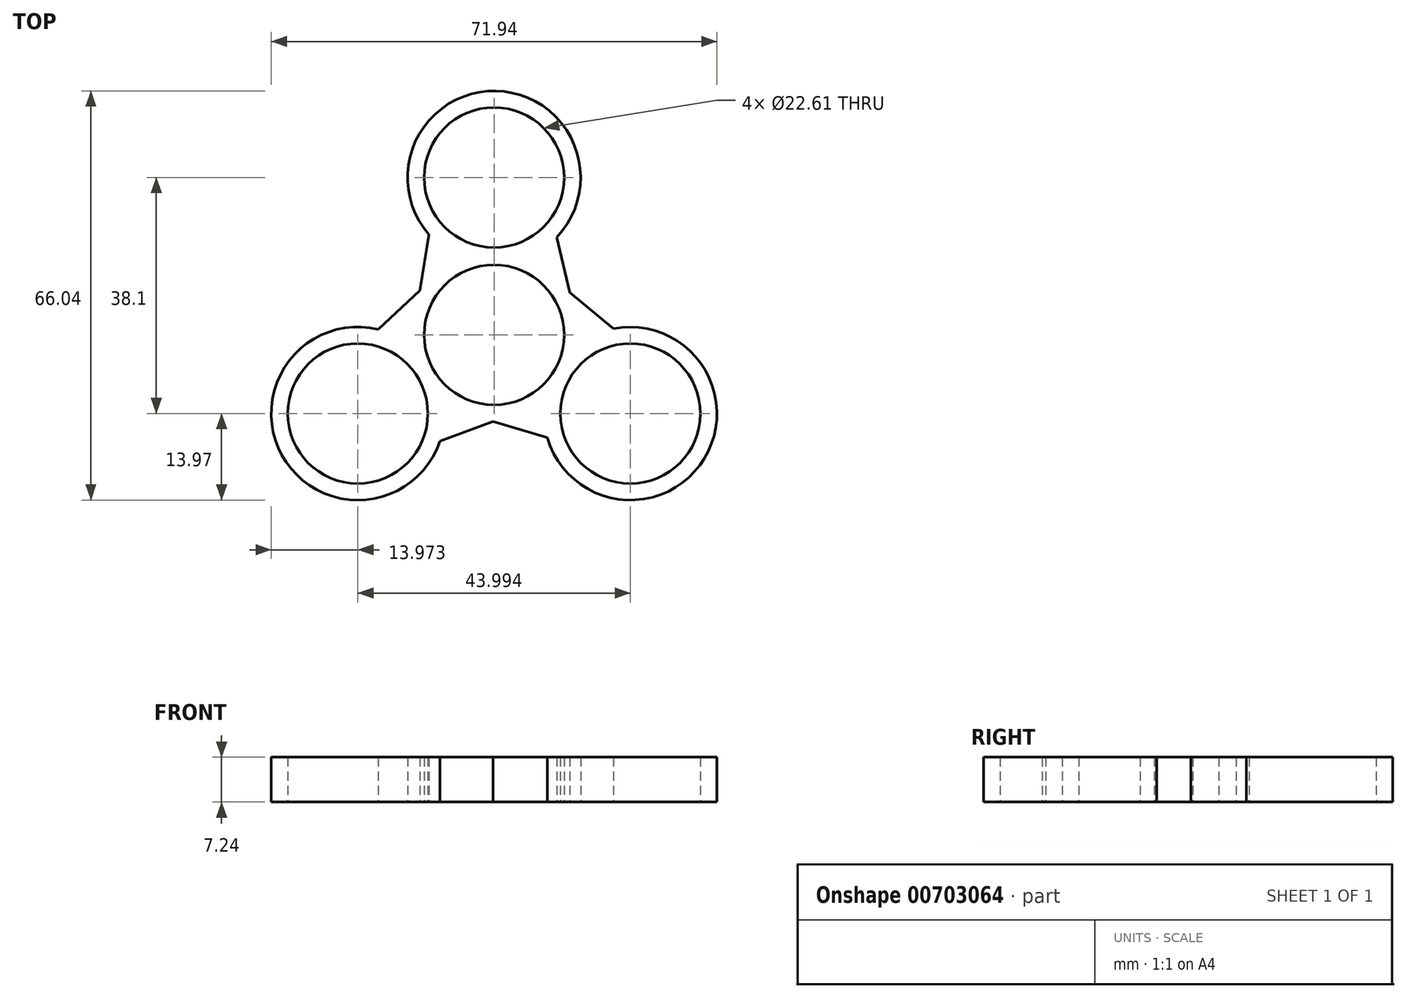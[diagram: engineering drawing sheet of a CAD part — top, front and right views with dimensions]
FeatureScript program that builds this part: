
annotation { "Feature Type Name" : "Feature", "Feature Type Description" : "" }
export const myFeature = defineFeature(function(context is Context, id is Id, definition is map)
    precondition{}
    {
        {
            var Q0;
            Q0=qCreatedBy(makeId("Top.planeOp"),FACE);
            var sketch = newSketch(context, id + "F0", { "sketchPlane" : qUnion([Q0])});
            skCircle(sketch, "E0", {"center": v(0, 25.4) * mm, "radius": 11.3 * mm});
            skCircle(sketch, "E1.1.0", {"center": v(-22, -12.7) * mm, "radius": 11.3 * mm});
            skCircle(sketch, "E1.2.0", {"center": v(22, -12.7) * mm, "radius": 11.3 * mm});
            skPoint(sketch, "E1.center", {"position": v(0, 0) * mm});
            skCircle(sketch, "E2", {"center": v(0, 0) * mm, "radius": 13.97 * mm});
            skPoint(sketch, "E3", {"position": v(-12, 7.14) * mm});
            skPoint(sketch, "E4", {"position": v(-10.18, 18.03) * mm});
            skPoint(sketch, "E5", {"position": v(-19.93, -0.3) * mm});
            skPoint(sketch, "E6.1.0", {"position": v(-10.53, -17.83) * mm});
            skPoint(sketch, "E6.1.1", {"position": v(-0.18, -13.97) * mm});
            skPoint(sketch, "E6.1.2", {"position": v(10.23, -17.1) * mm});
            skPoint(sketch, "E6.2.0", {"position": v(20.7, -0.2) * mm});
            skPoint(sketch, "E6.2.1", {"position": v(12.19, 6.83) * mm});
            skPoint(sketch, "E6.2.2", {"position": v(9.7, 17.42) * mm});
            skLineSegment(sketch, "E7", {"start": v(-12, 7.14) * mm, "end": v(-10.18, 18.03) * mm});
            skLineSegment(sketch, "E8", {"start": v(-12, 7.14) * mm, "end": v(-19.93, -0.3) * mm});
            skLineSegment(sketch, "E9", {"start": v(-10.53, -17.83) * mm, "end": v(-0.18, -13.97) * mm});
            skLineSegment(sketch, "E10", {"start": v(-0.18, -13.97) * mm, "end": v(10.23, -17.1) * mm});
            skLineSegment(sketch, "E11", {"start": v(20.7, -0.2) * mm, "end": v(12.19, 6.83) * mm});
            skLineSegment(sketch, "E12", {"start": v(9.7, 17.42) * mm, "end": v(12.19, 6.83) * mm});
            skCircle(sketch, "E13", {"center": v(0, 0) * mm, "radius": 11.3 * mm});
            skCircle(sketch, "E14", {"center": v(0, 25.4) * mm, "radius": 13.97 * mm});
            skCircle(sketch, "E15.1.0", {"center": v(-22, -12.7) * mm, "radius": 13.97 * mm});
            skCircle(sketch, "E15.2.0", {"center": v(22, -12.7) * mm, "radius": 13.97 * mm});
            skSolve(sketch);
        }
        {
            var Q0;
            Q0=makeQuery(id+"F0.imprint","IMPRINT",FACE,{"disambiguationData":[TD([[makeQuery(id+"F0.imprint","IMPRINT",EDGE,{"derivedFrom":sQuery(id+"F0.wireOp",EDGE,"E0")}),-1.0]])]});
            var Q1;
            {var subQ0=sQuery(id+"F0.wireOp",EDGE,"gAJnjUwW-bYsI-lxhw-ExFC-0EqGxPt0lFPb");Q1=makeQuery(id+"F0.imprint","IMPRINT",FACE,{"disambiguationData":[TD([[makeQuery(id+"F0.imprint","IMPRINT",EDGE,{"derivedFrom":subQ0}),1.0]])]});}
            var Q2;
            {var subQ0=sQuery(id+"F0.wireOp",EDGE,"cbf1ee79-b63b-43e7-bdae-fea5953c93ed.1.1");Q2=makeQuery(id+"F0.imprint","IMPRINT",FACE,{"disambiguationData":[TD([[makeQuery(id+"F0.imprint","IMPRINT",EDGE,{"derivedFrom":subQ0}),1.0]])]});}
            var Q3;
            Q3=makeQuery(id+"F0.imprint","IMPRINT",FACE,{"disambiguationData":[TD([[makeQuery(id+"F0.imprint","IMPRINT",EDGE,{"derivedFrom":sQuery(id+"F0.wireOp",EDGE,"LQtzWtV1-cpov-eoDI-daBr-TH9JdLP4XcMI")}),-1.0]])]});
            var Q4;
            Q4=makeQuery(id+"F0.imprint","IMPRINT",FACE,{"disambiguationData":[TD([[makeQuery(id+"F0.imprint","IMPRINT",EDGE,{"derivedFrom":sQuery(id+"F0.wireOp",EDGE,"LQtzWtV1-cpov-eoDI-daBr-TH9JdLP4XcMI")}),1.0]])]});
            var Q5;
            Q5=makeQuery(id+"F0.imprint","IMPRINT",FACE,{"disambiguationData":[TD([[makeQuery(id+"F0.imprint","IMPRINT",EDGE,{"derivedFrom":sQuery(id+"F0.wireOp",EDGE,"E1.2.0")}),-1.0]])]});
            var Q6;
            Q6=makeQuery(id+"F0.imprint","IMPRINT",FACE,{"disambiguationData":[TD([[makeQuery(id+"F0.imprint","IMPRINT",EDGE,{"derivedFrom":sQuery(id+"F0.wireOp",EDGE,"E1.1.0")}),-1.0]])]});
            var Q7;
            {var subQ0=sQuery(id+"F0.wireOp",EDGE,"XxgCCsIO-ZqaA-fPwp-7T2X-JmL23n1TTZja");Q7=makeQuery(id+"F0.imprint","IMPRINT",FACE,{"disambiguationData":[TD([[makeQuery(id+"F0.imprint","IMPRINT",EDGE,{"derivedFrom":subQ0}),1.0]])]});}
            var Q8;
            Q8=makeQuery(id+"F0.imprint","IMPRINT",FACE,{"disambiguationData":[TD([[makeQuery(id+"F0.imprint","IMPRINT",EDGE,{"derivedFrom":sQuery(id+"F0.wireOp",EDGE,"E13")}),-1.0]])]});
            var Q9;
            {var subQ0=sQuery(id+"F0.wireOp",EDGE,"E8");Q9=makeQuery(id+"F0.imprint","IMPRINT",FACE,{"disambiguationData":[TD([[makeQuery(id+"F0.imprint","IMPRINT",EDGE,{"derivedFrom":subQ0}),1.0]])]});}
            var Q10;
            {var subQ0=sQuery(id+"F0.wireOp",EDGE,"E7");Q10=makeQuery(id+"F0.imprint","IMPRINT",FACE,{"disambiguationData":[TD([[makeQuery(id+"F0.imprint","IMPRINT",EDGE,{"derivedFrom":subQ0}),-1.0]])]});}
            var Q11;
            {var subQ0=sQuery(id+"F0.wireOp",EDGE,"E12");Q11=makeQuery(id+"F0.imprint","IMPRINT",FACE,{"disambiguationData":[TD([[makeQuery(id+"F0.imprint","IMPRINT",EDGE,{"derivedFrom":subQ0}),-1.0]])]});}
            var Q12;
            {var subQ0=sQuery(id+"F0.wireOp",EDGE,"E11");Q12=makeQuery(id+"F0.imprint","IMPRINT",FACE,{"disambiguationData":[TD([[makeQuery(id+"F0.imprint","IMPRINT",EDGE,{"derivedFrom":subQ0}),1.0]])]});}
            var Q13;
            {var subQ0=sQuery(id+"F0.wireOp",EDGE,"E10");Q13=makeQuery(id+"F0.imprint","IMPRINT",FACE,{"disambiguationData":[TD([[makeQuery(id+"F0.imprint","IMPRINT",EDGE,{"derivedFrom":subQ0}),1.0]])]});}
            var Q14;
            {var subQ0=sQuery(id+"F0.wireOp",EDGE,"E9");Q14=makeQuery(id+"F0.imprint","IMPRINT",FACE,{"disambiguationData":[TD([[makeQuery(id+"F0.imprint","IMPRINT",EDGE,{"derivedFrom":subQ0}),1.0]])]});}
            var Q15;
            {var subQ0=sQuery(id+"F0.wireOp",EDGE,"E2");var subQ1=sQuery(id+"F0.wireOp",EDGE,"oYZP1axk-Xy9e-DZ7p-ojNj-aC0LJb1eXSLL");var subQ2=makeQuery(id+"F0.imprint","INTERSECT",VERTEX,{"disambiguationData":[OD(0.0)],"derivedFrom":[subQ1,subQ0]});Q15=makeQuery(id+"F0.imprint","IMPRINT",FACE,{"disambiguationData":[TD([[makeQuery(id+"F0.imprint","IMPRINT",EDGE,{"disambiguationData":[TD([[subQ2,-1.0]])],"derivedFrom":subQ1}),1.0]])]});}
            var Q16;
            {var subQ0=sQuery(id+"F0.wireOp",EDGE,"E2");var subQ1=sQuery(id+"F0.wireOp",EDGE,"E1.2.1");var subQ2=makeQuery(id+"F0.imprint","INTERSECT",VERTEX,{"disambiguationData":[OD(0.0)],"derivedFrom":[subQ1,subQ0]});Q16=makeQuery(id+"F0.imprint","IMPRINT",FACE,{"disambiguationData":[TD([[makeQuery(id+"F0.imprint","IMPRINT",EDGE,{"disambiguationData":[TD([[subQ2,-1.0]])],"derivedFrom":subQ1}),1.0]])]});}
            var Q17;
            {var subQ0=sQuery(id+"F0.wireOp",EDGE,"E2");var subQ1=sQuery(id+"F0.wireOp",EDGE,"E1.1.1");var subQ2=makeQuery(id+"F0.imprint","INTERSECT",VERTEX,{"disambiguationData":[OD(0.0)],"derivedFrom":[subQ1,subQ0]});Q17=makeQuery(id+"F0.imprint","IMPRINT",FACE,{"disambiguationData":[TD([[makeQuery(id+"F0.imprint","IMPRINT",EDGE,{"disambiguationData":[TD([[subQ2,-1.0]])],"derivedFrom":subQ1}),1.0]])]});}
            var Q18;
            {var subQ0=sQuery(id+"F0.wireOp",EDGE,"E15.2.0");var subQ1=sQuery(id+"F0.wireOp",EDGE,"E2");var subQ2=makeQuery(id+"F0.imprint","INTERSECT",VERTEX,{"disambiguationData":[OD(0.0)],"derivedFrom":[subQ1,subQ0]});Q18=makeQuery(id+"F0.imprint","IMPRINT",FACE,{"disambiguationData":[TD([[makeQuery(id+"F0.imprint","IMPRINT",EDGE,{"disambiguationData":[TD([[subQ2,-1.0]])],"derivedFrom":subQ1}),1.0]])]});}
            var Q19;
            {var subQ0=sQuery(id+"F0.wireOp",EDGE,"E14");var subQ1=sQuery(id+"F0.wireOp",EDGE,"E2");var subQ2=makeQuery(id+"F0.imprint","INTERSECT",VERTEX,{"disambiguationData":[OD(0.0)],"derivedFrom":[subQ1,subQ0]});Q19=makeQuery(id+"F0.imprint","IMPRINT",FACE,{"disambiguationData":[TD([[makeQuery(id+"F0.imprint","IMPRINT",EDGE,{"disambiguationData":[TD([[subQ2,-1.0]])],"derivedFrom":subQ1}),1.0]])]});}
            var Q20;
            {var subQ0=sQuery(id+"F0.wireOp",EDGE,"E15.1.0");var subQ1=sQuery(id+"F0.wireOp",EDGE,"E2");var subQ2=makeQuery(id+"F0.imprint","INTERSECT",VERTEX,{"disambiguationData":[OD(0.0)],"derivedFrom":[subQ1,subQ0]});Q20=makeQuery(id+"F0.imprint","IMPRINT",FACE,{"disambiguationData":[TD([[makeQuery(id+"F0.imprint","IMPRINT",EDGE,{"disambiguationData":[TD([[subQ2,-1.0]])],"derivedFrom":subQ1}),1.0]])]});}
            extrude(context, id + "F1", {"entities" : qUnion([Q0, Q1, Q2, Q3, Q4, Q5, Q6, Q7, Q8, Q9, Q10, Q11, Q12, Q13, Q14, Q15, Q16, Q17, Q18, Q19, Q20]), "depth" : 7.24 * mm, "offsetDistance" : 25.4 * mm});
        }
    });
